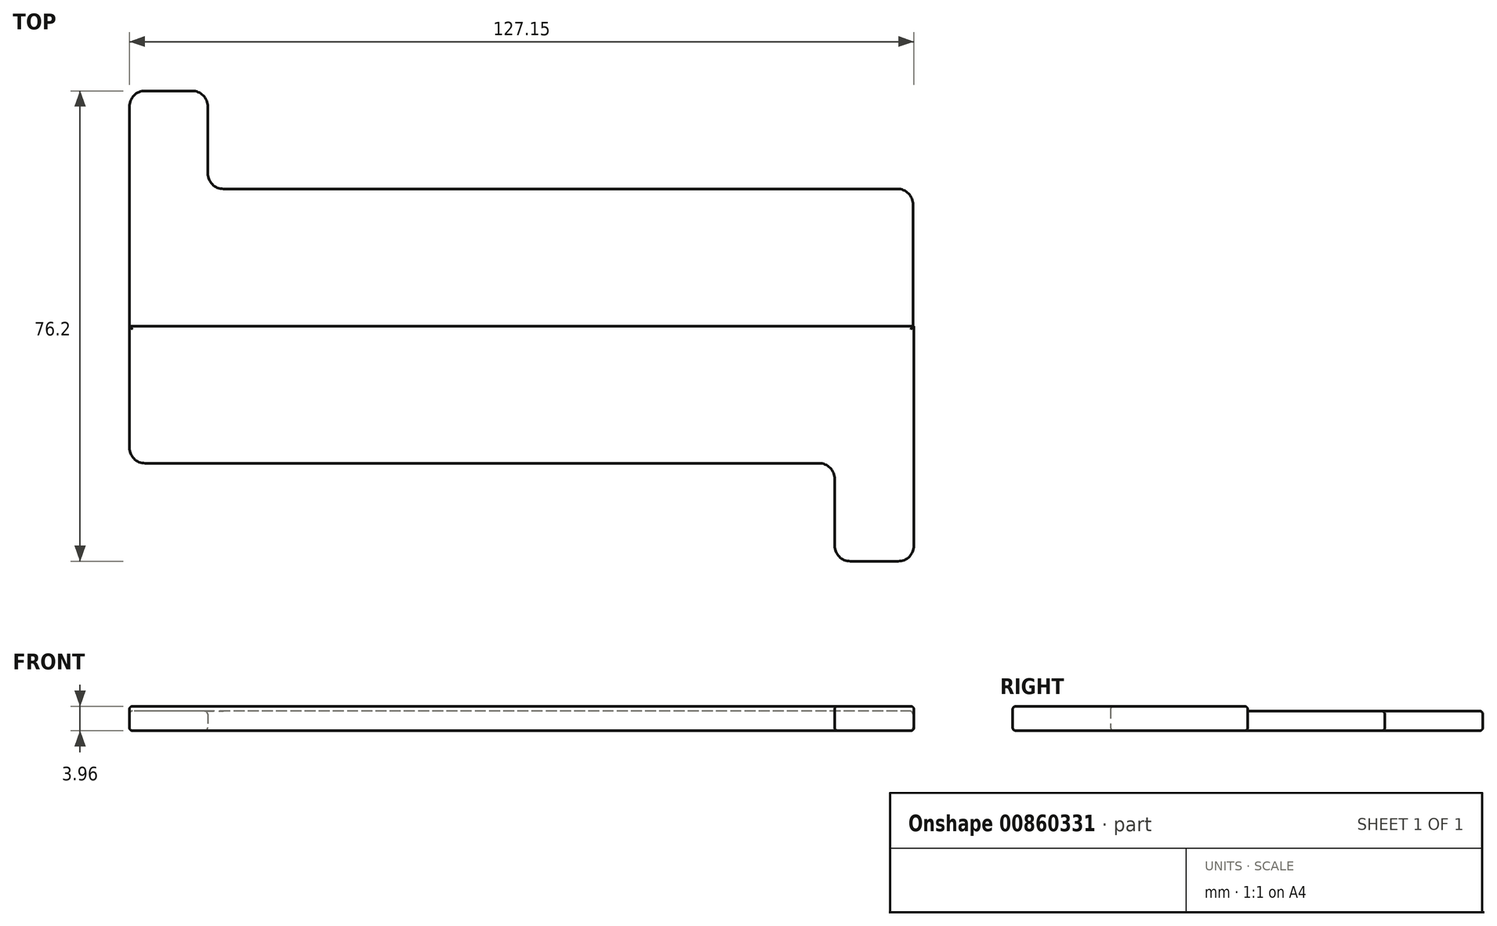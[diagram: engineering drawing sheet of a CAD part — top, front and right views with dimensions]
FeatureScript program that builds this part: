
annotation { "Feature Type Name" : "Feature", "Feature Type Description" : "" }
export const myFeature = defineFeature(function(context is Context, id is Id, definition is map)
    precondition{}
    {
        {
            var Q0;
            Q0=qCreatedBy(makeId("Top.planeOp"),FACE);
            var sketch = newSketch(context, id + "F0", { "sketchPlane" : qUnion([Q0])});
            skLineSegment(sketch, "E0.bottom", {"start": v(63.5, -19.05) * mm, "end": v(-63.5, -19.05) * mm});
            skLineSegment(sketch, "E0.top", {"start": v(-50.8, 19.05) * mm, "end": v(-63.5, 19.05) * mm});
            skLineSegment(sketch, "E0.left", {"start": v(63.5, -19.05) * mm, "end": v(63.5, 3.18) * mm});
            skLineSegment(sketch, "E0.right", {"start": v(-63.5, -19.05) * mm, "end": v(-63.5, 19.05) * mm});
            skPoint(sketch, "E0.middle", {"position": v(0, 0) * mm});
            skLineSegment(sketch, "E1.top", {"start": v(63.5, 3.18) * mm, "end": v(-50.8, 3.17) * mm});
            skLineSegment(sketch, "E1.right", {"start": v(-50.8, 19.05) * mm, "end": v(-50.8, 3.17) * mm});
            skPoint(sketch, "E2.orphan", {"position": v(63.5, 19.05) * mm});
            skLineSegment(sketch, "E3.bottom", {"start": v(-63.5, -19.05) * mm, "end": v(63.65, -19.05) * mm});
            skLineSegment(sketch, "E3.top", {"start": v(50.8, -57.15) * mm, "end": v(63.65, -57.15) * mm});
            skLineSegment(sketch, "E3.left", {"start": v(-63.5, -19.05) * mm, "end": v(-63.5, -41.27) * mm});
            skLineSegment(sketch, "E3.right", {"start": v(63.65, -19.05) * mm, "end": v(63.65, -57.15) * mm});
            skLineSegment(sketch, "E4.top", {"start": v(-63.5, -41.27) * mm, "end": v(50.8, -41.27) * mm});
            skLineSegment(sketch, "E4.right", {"start": v(50.8, -57.15) * mm, "end": v(50.8, -41.27) * mm});
            skSolve(sketch);
        }
        {
            var Q0;
            Q0=makeQuery(id+"F0.imprint","IMPRINT",FACE,{"disambiguationData":[TD([[makeQuery(id+"F0.imprint","IMPRINT",EDGE,{"derivedFrom":sQuery(id+"F0.wireOp",EDGE,"E0.bottom")}),-1.0]])]});
            extrude(context, id + "F1", {"entities" : qUnion([Q0]), "depth" : 3.17 * mm, "offsetDistance" : 25.4 * mm});
        }
        {
            var Q0;
            Q0=makeQuery(id+"F0.imprint","IMPRINT",FACE,{"disambiguationData":[TD([[makeQuery(id+"F0.imprint","IMPRINT",EDGE,{"derivedFrom":sQuery(id+"F0.wireOp",EDGE,"E0.bottom")}),1.0]])]});
            extrude(context, id + "F2", {"entities" : qUnion([Q0]), "operationType" : NewBodyOperationType.ADD, "depth" : 3.96 * mm, "offsetDistance" : 25.4 * mm});
        }
        {
            var Q0;
            Q0=makeQuery(id+"F2.opExtrude","SWEPT_EDGE",EDGE,{"disambiguationData":[OSD([sQuery(id+"F0.wireOp",EDGE,"E3.left"),sQuery(id+"F0.wireOp",EDGE,"E4.top")])]});
            var Q1;
            Q1=makeQuery(id+"F2.opExtrude","SWEPT_EDGE",EDGE,{"disambiguationData":[OSD([sQuery(id+"F0.wireOp",EDGE,"E4.top"),sQuery(id+"F0.wireOp",EDGE,"E4.right")])]});
            var Q2;
            Q2=makeQuery(id+"F2.opExtrude","SWEPT_EDGE",EDGE,{"disambiguationData":[OSD([sQuery(id+"F0.wireOp",EDGE,"E3.top"),sQuery(id+"F0.wireOp",EDGE,"E4.right")])]});
            var Q3;
            Q3=makeQuery(id+"F2.opExtrude","SWEPT_EDGE",EDGE,{"disambiguationData":[OSD([sQuery(id+"F0.wireOp",EDGE,"E3.top"),sQuery(id+"F0.wireOp",EDGE,"E3.right")])]});
            var Q4;
            Q4=makeQuery(id+"F1.opExtrude","SWEPT_EDGE",EDGE,{"disambiguationData":[OSD([sQuery(id+"F0.wireOp",EDGE,"E0.left"),sQuery(id+"F0.wireOp",EDGE,"E1.top")])]});
            var Q5;
            Q5=makeQuery(id+"F1.opExtrude","SWEPT_EDGE",EDGE,{"disambiguationData":[OSD([sQuery(id+"F0.wireOp",EDGE,"E1.top"),sQuery(id+"F0.wireOp",EDGE,"E1.right")])]});
            var Q6;
            Q6=makeQuery(id+"F1.opExtrude","SWEPT_EDGE",EDGE,{"disambiguationData":[OSD([sQuery(id+"F0.wireOp",EDGE,"E0.top"),sQuery(id+"F0.wireOp",EDGE,"E1.right")])]});
            var Q7;
            Q7=makeQuery(id+"F1.opExtrude","SWEPT_EDGE",EDGE,{"disambiguationData":[OSD([sQuery(id+"F0.wireOp",EDGE,"E0.top"),sQuery(id+"F0.wireOp",EDGE,"E0.right")])]});
            fillet(context, id + "F3", {"entities" : qUnion([Q0, Q1, Q2, Q3, Q4, Q5, Q6, Q7]), "radius" : 2.54 * mm, "tangentPropagation" : true, "allowEdgeOverflow" : false});
        }
        {
            var Q0;
            Q0=makeQuery(id+"F2.opExtrude","CAP_FACE",FACE,{"disambiguationData":[OSD([sQuery(id+"F0.wireOp",EDGE,"E0.bottom"),sQuery(id+"F0.wireOp",EDGE,"E3.bottom"),sQuery(id+"F0.wireOp",EDGE,"E3.top"),sQuery(id+"F0.wireOp",EDGE,"E3.left"),sQuery(id+"F0.wireOp",EDGE,"E3.right"),sQuery(id+"F0.wireOp",EDGE,"E4.top"),sQuery(id+"F0.wireOp",EDGE,"E4.right")])],"isStart":false});
            var Q1;
            Q1=makeQuery(id+"F1.opExtrude","CAP_EDGE",EDGE,{"disambiguationData":[OSD([sQuery(id+"F0.wireOp",EDGE,"E0.left")])],"isStart":false});
            var Q2;
            {var subQ0=sQuery(id+"F0.wireOp",EDGE,"E0.bottom");Q2=makeQuery(id+"F2.boolean.opBoolean","MERGE",FACE,{"derivedFrom":[makeQuery(id+"F1.opExtrude","CAP_FACE",FACE,{"disambiguationData":[OSD([subQ0,sQuery(id+"F0.wireOp",EDGE,"E0.top"),sQuery(id+"F0.wireOp",EDGE,"E0.left"),sQuery(id+"F0.wireOp",EDGE,"E0.right"),sQuery(id+"F0.wireOp",EDGE,"E1.top"),sQuery(id+"F0.wireOp",EDGE,"E1.right")])],"isStart":true}),makeQuery(id+"F2.opExtrude","CAP_FACE",FACE,{"disambiguationData":[OSD([subQ0,sQuery(id+"F0.wireOp",EDGE,"E3.bottom"),sQuery(id+"F0.wireOp",EDGE,"E3.top"),sQuery(id+"F0.wireOp",EDGE,"E3.left"),sQuery(id+"F0.wireOp",EDGE,"E3.right"),sQuery(id+"F0.wireOp",EDGE,"E4.top"),sQuery(id+"F0.wireOp",EDGE,"E4.right")])],"isStart":true})]});}
            fillet(context, id + "F4", {"entities" : qUnion([Q0, Q1, Q2]), "radius" : 0.5 * mm, "tangentPropagation" : true, "allowEdgeOverflow" : false});
        }
    });
